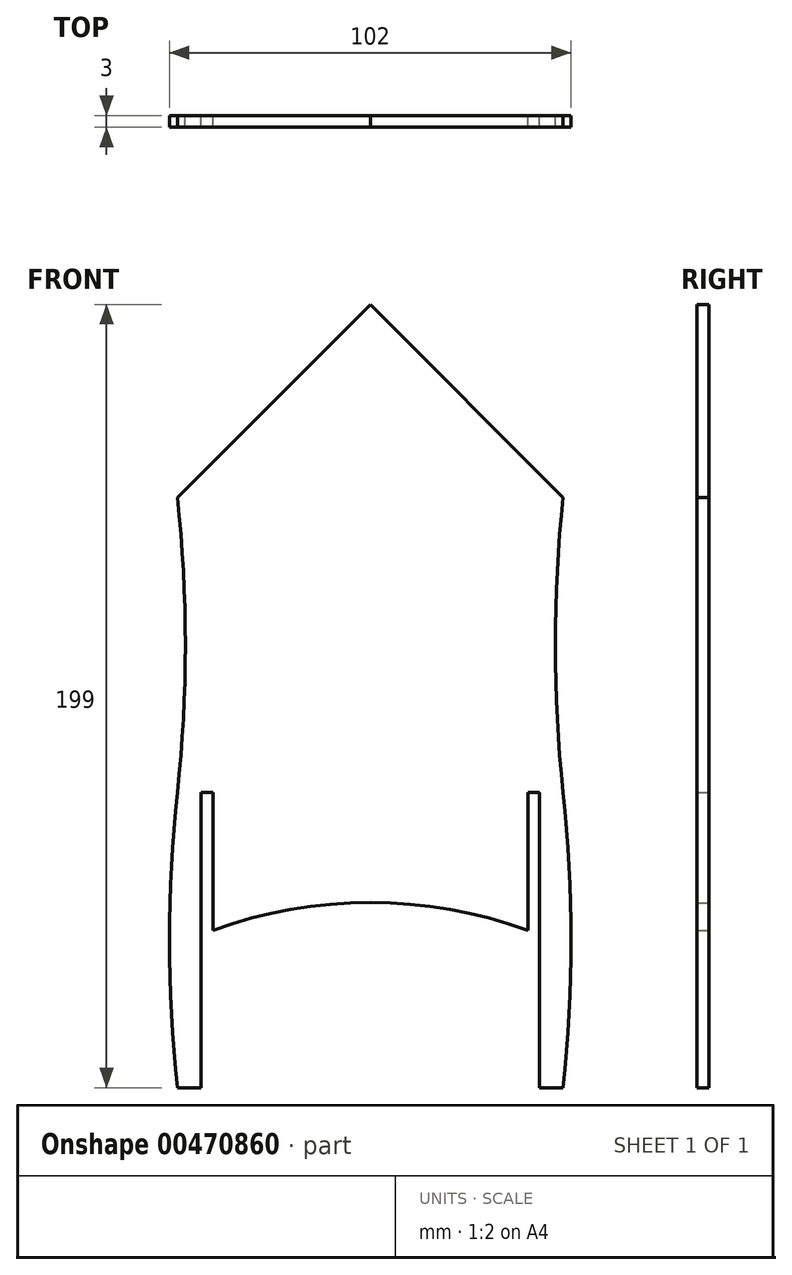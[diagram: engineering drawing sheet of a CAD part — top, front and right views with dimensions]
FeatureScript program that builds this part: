
annotation { "Feature Type Name" : "Feature", "Feature Type Description" : "" }
export const myFeature = defineFeature(function(context is Context, id is Id, definition is map)
    precondition{}
    {
        {
            assignVariable(context, id + "F0", {"name" : "WoodWidth", "anyValue" : 3});
        }
        {
            var Q0;
            Q0=qCreatedBy(makeId("Front.planeOp"),FACE);
            var sketch = newSketch(context, id + "F1", { "sketchPlane" : qUnion([Q0])});
            skLineSegment(sketch, "E0.bottom", {"start": v(49, -75) * mm, "end": v(-49, -75) * mm});
            skLineSegment(sketch, "E0.top", {"start": v(49, 75) * mm, "end": v(-49, 75) * mm});
            skLineSegment(sketch, "E0.left", {"start": v(49, -75) * mm, "end": v(49, 75) * mm});
            skLineSegment(sketch, "E0.right", {"start": v(-49, -75) * mm, "end": v(-49, 75) * mm});
            skPoint(sketch, "E0.middle", {"position": v(0, 0) * mm});
            skLineSegment(sketch, "E1.bottom", {"start": v(-43, -75) * mm, "end": v(-40, -75) * mm});
            skLineSegment(sketch, "E1.top", {"start": v(-43, 0) * mm, "end": v(-40, 0) * mm});
            skLineSegment(sketch, "E1.left", {"start": v(-43, -75) * mm, "end": v(-43, 0) * mm});
            skLineSegment(sketch, "E1.right", {"start": v(-40, -75) * mm, "end": v(-40, 0) * mm});
            skLineSegment(sketch, "E2.bottom", {"start": v(40, -75) * mm, "end": v(43, -75) * mm});
            skLineSegment(sketch, "E2.top", {"start": v(40, 0) * mm, "end": v(43, 0) * mm});
            skLineSegment(sketch, "E2.left", {"start": v(40, -75) * mm, "end": v(40, 0) * mm});
            skLineSegment(sketch, "E2.right", {"start": v(43, -75) * mm, "end": v(43, 0) * mm});
            skLineSegment(sketch, "E3.bottom", {"start": v(-40, -75) * mm, "end": v(-25, -75) * mm});
            skLineSegment(sketch, "E3.top", {"start": v(-40, -78) * mm, "end": v(-25, -78) * mm});
            skLineSegment(sketch, "E3.left", {"start": v(-40, -75) * mm, "end": v(-40, -78) * mm});
            skLineSegment(sketch, "E3.right", {"start": v(-25, -75) * mm, "end": v(-25, -78) * mm});
            skLineSegment(sketch, "E4.bottom", {"start": v(40, -75) * mm, "end": v(25, -75) * mm});
            skLineSegment(sketch, "E4.top", {"start": v(40, -78) * mm, "end": v(25, -78) * mm});
            skLineSegment(sketch, "E4.left", {"start": v(40, -75) * mm, "end": v(40, -78) * mm});
            skLineSegment(sketch, "E4.right", {"start": v(25, -75) * mm, "end": v(25, -78) * mm});
            skLineSegment(sketch, "E5.bottom", {"start": v(-49, -75) * mm, "end": v(-43, -75) * mm});
            skLineSegment(sketch, "E5.top", {"start": v(-49, -78) * mm, "end": v(-43, -78) * mm});
            skLineSegment(sketch, "E5.left", {"start": v(-49, -75) * mm, "end": v(-49, -78) * mm});
            skLineSegment(sketch, "E5.right", {"start": v(-43, -75) * mm, "end": v(-43, -78) * mm});
            skLineSegment(sketch, "E6.bottom", {"start": v(43, -75) * mm, "end": v(49, -75) * mm});
            skLineSegment(sketch, "E6.top", {"start": v(43, -78) * mm, "end": v(49, -78) * mm});
            skLineSegment(sketch, "E6.left", {"start": v(43, -75) * mm, "end": v(43, -78) * mm});
            skLineSegment(sketch, "E6.right", {"start": v(49, -75) * mm, "end": v(49, -78) * mm});
            skLineSegment(sketch, "E7", {"start": v(-49, 75) * mm, "end": v(0, 124) * mm});
            skLineSegment(sketch, "E8", {"start": v(0, 124) * mm, "end": v(49, 75) * mm});
            skLineSegment(sketch, "E9", {"start": v(-40, -35) * mm, "end": v(40, -35) * mm});
            skArc(sketch, "E10", {"start": v(40, -35) * mm, "mid": v(0, -28) * mm, "end": v(-40, -35) * mm});
            skArc(sketch, "E11", {"start": v(-49, 0) * mm, "mid": v(-51, -37.5) * mm, "end": v(-49, -75) * mm});
            skArc(sketch, "E12", {"start": v(-49, 0) * mm, "mid": v(-47, 37.5) * mm, "end": v(-49, 75) * mm});
            skArc(sketch, "E13", {"start": v(49, -75) * mm, "mid": v(51, -37.5) * mm, "end": v(49, 0) * mm});
            skArc(sketch, "E14", {"start": v(49, 75) * mm, "mid": v(47, 37.5) * mm, "end": v(49, 0) * mm});
            skSolve(sketch);
        }
        {
            var Q0;
            Q0=makeQuery(id+"F1.imprint","IMPRINT",FACE,{"disambiguationData":[TD([[makeQuery(id+"F1.imprint","IMPRINT",EDGE,{"derivedFrom":sQuery(id+"F1.wireOp",EDGE,"E0.top")}),-1.0]])]});
            var Q1;
            Q1=makeQuery(id+"F1.imprint","IMPRINT",FACE,{"disambiguationData":[TD([[makeQuery(id+"F1.imprint","IMPRINT",EDGE,{"derivedFrom":sQuery(id+"F1.wireOp",EDGE,"E0.top")}),1.0]])]});
            var Q2;
            Q2=makeQuery(id+"F1.imprint","IMPRINT",FACE,{"disambiguationData":[TD([[makeQuery(id+"F1.imprint","IMPRINT",EDGE,{"derivedFrom":sQuery(id+"F1.wireOp",EDGE,"E5.bottom")}),-1.0]])]});
            var Q3;
            Q3=makeQuery(id+"F1.imprint","IMPRINT",FACE,{"disambiguationData":[TD([[makeQuery(id+"F1.imprint","IMPRINT",EDGE,{"derivedFrom":sQuery(id+"F1.wireOp",EDGE,"E6.bottom")}),-1.0]])]});
            var Q4;
            {var subQ0=sQuery(id+"F1.wireOp",EDGE,"E11");Q4=makeQuery(id+"F1.imprint","IMPRINT",FACE,{"disambiguationData":[TD([[makeQuery(id+"F1.imprint","IMPRINT",EDGE,{"derivedFrom":subQ0}),1.0]])]});}
            var Q5;
            {var subQ0=sQuery(id+"F1.wireOp",EDGE,"E13");Q5=makeQuery(id+"F1.imprint","IMPRINT",FACE,{"disambiguationData":[TD([[makeQuery(id+"F1.imprint","IMPRINT",EDGE,{"derivedFrom":subQ0}),1.0]])]});}
            extrude(context, id + "F2", {"entities" : qUnion([Q0, Q1, Q2, Q3, Q4, Q5]), "depth" : (getVariable(context, 'WoodWidth')) * mm});
        }
    });
